# Revit family: VTp704 Муфта переходная
name_source: partatom
category: Соединительные детали трубопроводов
revit_build: Autodesk Revit 2015 (Build: 20140606_1530(x64)
units: mm (PartAtom-declared; Revit-internal decimal feet)

## types (19) — shared parameters
Группа модели = VTp.700
Изготовитель = VALTEC S.R.L.
Коэффициент K = 0.5
Метод определения потерь = Коэффициент K
Описание = Муфта переходная (труба-раструб)
Таблица коэффициентов K = Angle Valve Threaded

## per-type parameters (varying)
- 25-20: 25-20=Да; 32-20=Нет; 32-25=Нет; 40-20=Нет; 40-25=Нет; 40-32=Нет; 50-20=Нет; 50-25=Нет; 50-32=Нет; 50-40=Нет; 63-20=Нет; 63-25=Нет; 63-32=Нет; 63-40=Нет; 63-50=Нет; 75-50=Нет; 75-63=Нет; 90-63=Нет; 90-75=Нет; A=36 мм; B=15 мм; C=16 мм; d1=25 мм; d2=20 мм; Код по классификатору=VTp.704.0.025020
- 32-25: 25-20=Нет; 32-20=Нет; 32-25=Да; 40-20=Нет; 40-25=Нет; 40-32=Нет; 50-20=Нет; 50-25=Нет; 50-32=Нет; 50-40=Нет; 63-20=Нет; 63-25=Нет; 63-32=Нет; 63-40=Нет; 63-50=Нет; 75-50=Нет; 75-63=Нет; 90-63=Нет; 90-75=Нет; A=39 мм; B=19 мм; C=19 мм; d1=32 мм; d2=25 мм; Код по классификатору=VTp.704.0.032025
- 40-20: 25-20=Нет; 32-20=Нет; 32-25=Нет; 40-20=Да; 40-25=Нет; 40-32=Нет; 50-20=Нет; 50-25=Нет; 50-32=Нет; 50-40=Нет; 63-20=Нет; 63-25=Нет; 63-32=Нет; 63-40=Нет; 63-50=Нет; 75-50=Нет; 75-63=Нет; 90-63=Нет; 90-75=Нет; A=40 мм; B=21 мм; C=13 мм; d1=40 мм; d2=20 мм; Код по классификатору=VTp.704.0.040020
- 32-20: 25-20=Нет; 32-20=Да; 32-25=Нет; 40-20=Нет; 40-25=Нет; 40-32=Нет; 50-20=Нет; 50-25=Нет; 50-32=Нет; 50-40=Нет; 63-20=Нет; 63-25=Нет; 63-32=Нет; 63-40=Нет; 63-50=Нет; 75-50=Нет; 75-63=Нет; 90-63=Нет; 90-75=Нет; A=34 мм; B=19 мм; C=13 мм; d1=32 мм; d2=20 мм; Код по классификатору=VTp.704.0.032020
- 50-20: 25-20=Нет; 32-20=Нет; 32-25=Нет; 40-20=Нет; 40-25=Нет; 40-32=Нет; 50-20=Да; 50-25=Нет; 50-32=Нет; 50-40=Нет; 63-20=Нет; 63-25=Нет; 63-32=Нет; 63-40=Нет; 63-50=Нет; 75-50=Нет; 75-63=Нет; 90-63=Нет; 90-75=Нет; A=41 мм; B=24 мм; C=10 мм; d1=50 мм; d2=20 мм; Код по классификатору=VTp.704.0.050020
- 63-20: 25-20=Нет; 32-20=Нет; 32-25=Нет; 40-20=Нет; 40-25=Нет; 40-32=Нет; 50-20=Нет; 50-25=Нет; 50-32=Нет; 50-40=Нет; 63-20=Да; 63-25=Нет; 63-32=Нет; 63-40=Нет; 63-50=Нет; 75-50=Нет; 75-63=Нет; 90-63=Нет; 90-75=Нет; A=47 мм; B=20 мм; C=9 мм; d1=63 мм; d2=20 мм; Код по классификатору=VTp.704.0.063020
- 75-50: 25-20=Нет; 32-20=Нет; 32-25=Нет; 40-20=Нет; 40-25=Нет; 40-32=Нет; 50-20=Нет; 50-25=Нет; 50-32=Нет; 50-40=Нет; 63-20=Нет; 63-25=Нет; 63-32=Нет; 63-40=Нет; 63-50=Нет; 75-50=Да; 75-63=Нет; 90-63=Нет; 90-75=Нет; A=54 мм; B=28 мм; C=25 мм; d1=75 мм; d2=50 мм; Код по классификатору=VTp.704.0.075050
- 40-25: 25-20=Нет; 32-20=Нет; 32-25=Нет; 40-20=Нет; 40-25=Да; 40-32=Нет; 50-20=Нет; 50-25=Нет; 50-32=Нет; 50-40=Нет; 63-20=Нет; 63-25=Нет; 63-32=Нет; 63-40=Нет; 63-50=Нет; 75-50=Нет; 75-63=Нет; 90-63=Нет; 90-75=Нет; A=38 мм; B=21 мм; C=14 мм; d1=40 мм; d2=25 мм; Код по классификатору=VTp.704.0.040025
- 40-32: 25-20=Нет; 32-20=Нет; 32-25=Нет; 40-20=Нет; 40-25=Нет; 40-32=Да; 50-20=Нет; 50-25=Нет; 50-32=Нет; 50-40=Нет; 63-20=Нет; 63-25=Нет; 63-32=Нет; 63-40=Нет; 63-50=Нет; 75-50=Нет; 75-63=Нет; 90-63=Нет; 90-75=Нет; A=44 мм; B=21 мм; C=21 мм; d1=40 мм; d2=32 мм; Код по классификатору=VTp.704.0.040032
- 50-25: 25-20=Нет; 32-20=Нет; 32-25=Нет; 40-20=Нет; 40-25=Нет; 40-32=Нет; 50-20=Нет; 50-25=Да; 50-32=Нет; 50-40=Нет; 63-20=Нет; 63-25=Нет; 63-32=Нет; 63-40=Нет; 63-50=Нет; 75-50=Нет; 75-63=Нет; 90-63=Нет; 90-75=Нет; A=48 мм; B=24 мм; C=18 мм; d1=50 мм; d2=25 мм; Код по классификатору=VTp.704.0.050025
- 50-32: 25-20=Нет; 32-20=Нет; 32-25=Нет; 40-20=Нет; 40-25=Нет; 40-32=Нет; 50-20=Нет; 50-25=Нет; 50-32=Да; 50-40=Нет; 63-20=Нет; 63-25=Нет; 63-32=Нет; 63-40=Нет; 63-50=Нет; 75-50=Нет; 75-63=Нет; 90-63=Нет; 90-75=Нет; A=49 мм; B=24 мм; C=22 мм; d1=50 мм; d2=32 мм; Код по классификатору=VTp.704.0.050032
- 50-40: 25-20=Нет; 32-20=Нет; 32-25=Нет; 40-20=Нет; 40-25=Нет; 40-32=Нет; 50-20=Нет; 50-25=Нет; 50-32=Нет; 50-40=Да; 63-20=Нет; 63-25=Нет; 63-32=Нет; 63-40=Нет; 63-50=Нет; 75-50=Нет; 75-63=Нет; 90-63=Нет; 90-75=Нет; A=50 мм; B=24 мм; C=23 мм; d1=50 мм; d2=40 мм; Код по классификатору=VTp.704.0.050040
- 63-25: 25-20=Нет; 32-20=Нет; 32-25=Нет; 40-20=Нет; 40-25=Нет; 40-32=Нет; 50-20=Нет; 50-25=Нет; 50-32=Нет; 50-40=Нет; 63-20=Нет; 63-25=Да; 63-32=Нет; 63-40=Нет; 63-50=Нет; 75-50=Нет; 75-63=Нет; 90-63=Нет; 90-75=Нет; A=54 мм; B=18 мм; C=18 мм; d1=63 мм; d2=25 мм; Код по классификатору=VTp.704.0.063025
- 63-32: 25-20=Нет; 32-20=Нет; 32-25=Нет; 40-20=Нет; 40-25=Нет; 40-32=Нет; 50-20=Нет; 50-25=Нет; 50-32=Нет; 50-40=Нет; 63-20=Нет; 63-25=Нет; 63-32=Да; 63-40=Нет; 63-50=Нет; 75-50=Нет; 75-63=Нет; 90-63=Нет; 90-75=Нет; A=56 мм; B=25 мм; C=18 мм; d1=63 мм; d2=32 мм; Код по классификатору=VTp.704.0.063032
- 63-40: 25-20=Нет; 32-20=Нет; 32-25=Нет; 40-20=Нет; 40-25=Нет; 40-32=Нет; 50-20=Нет; 50-25=Нет; 50-32=Нет; 50-40=Нет; 63-20=Нет; 63-25=Нет; 63-32=Нет; 63-40=Да; 63-50=Нет; 75-50=Нет; 75-63=Нет; 90-63=Нет; 90-75=Нет; A=54 мм; B=26 мм; C=20 мм; d1=63 мм; d2=40 мм; Код по классификатору=VTp.704.0.063040
- 63-50: 25-20=Нет; 32-20=Нет; 32-25=Нет; 40-20=Нет; 40-25=Нет; 40-32=Нет; 50-20=Нет; 50-25=Нет; 50-32=Нет; 50-40=Нет; 63-20=Нет; 63-25=Нет; 63-32=Нет; 63-40=Нет; 63-50=Да; 75-50=Нет; 75-63=Нет; 90-63=Нет; 90-75=Нет; A=58 мм; B=25 мм; C=22 мм; d1=63 мм; d2=50 мм; Код по классификатору=VTp.704.0.063050
- 75-63: 25-20=Нет; 32-20=Нет; 32-25=Нет; 40-20=Нет; 40-25=Нет; 40-32=Нет; 50-20=Нет; 50-25=Нет; 50-32=Нет; 50-40=Нет; 63-20=Нет; 63-25=Нет; 63-32=Нет; 63-40=Нет; 63-50=Нет; 75-50=Нет; 75-63=Да; 90-63=Нет; 90-75=Нет; A=71 мм; B=30 мм; C=25 мм; d1=75 мм; d2=63 мм; Код по классификатору=VTp.704.0.075063
- 90-63: 25-20=Нет; 32-20=Нет; 32-25=Нет; 40-20=Нет; 40-25=Нет; 40-32=Нет; 50-20=Нет; 50-25=Нет; 50-32=Нет; 50-40=Нет; 63-20=Нет; 63-25=Нет; 63-32=Нет; 63-40=Нет; 63-50=Нет; 75-50=Нет; 75-63=Нет; 90-63=Да; 90-75=Нет; A=69 мм; B=35 мм; C=28 мм; d1=90 мм; d2=63 мм; Код по классификатору=VTp.704.0.090063
- 90-75: 25-20=Нет; 32-20=Нет; 32-25=Нет; 40-20=Нет; 40-25=Нет; 40-32=Нет; 50-20=Нет; 50-25=Нет; 50-32=Нет; 50-40=Нет; 63-20=Нет; 63-25=Нет; 63-32=Нет; 63-40=Нет; 63-50=Нет; 75-50=Нет; 75-63=Нет; 90-63=Нет; 90-75=Да; A=78 мм; B=35 мм; C=30 мм; d1=90 мм; d2=75 мм; Код по классификатору=VTp.704.0.090075
